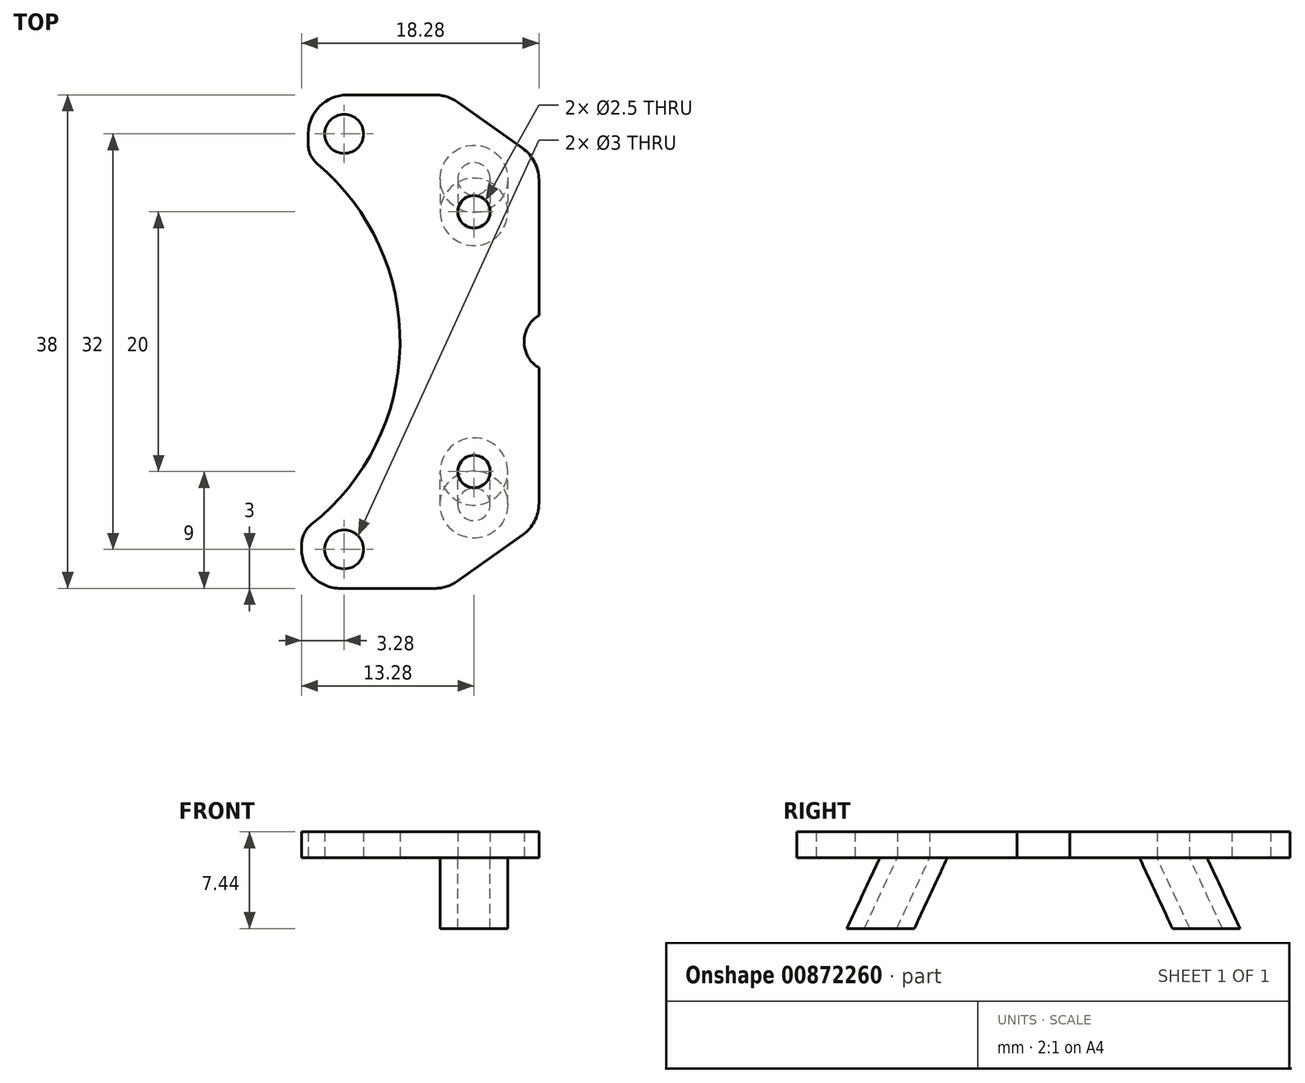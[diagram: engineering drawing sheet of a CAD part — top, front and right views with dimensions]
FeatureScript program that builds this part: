
annotation { "Feature Type Name" : "Feature", "Feature Type Description" : "" }
export const myFeature = defineFeature(function(context is Context, id is Id, definition is map)
    precondition{}
    {
        {
            var Q0;
            Q0=qCreatedBy(makeId("Top.planeOp"),FACE);
            var sketch = newSketch(context, id + "F0", { "sketchPlane" : qUnion([Q0])});
            skLineSegment(sketch, "E0.left", {"start": v(15, -12.45) * mm, "end": v(15, -2.03) * mm});
            skPoint(sketch, "E0.middle", {"position": v(0, 0) * mm});
            skPoint(sketch, "E1", {"position": v(0, 16) * mm});
            skPoint(sketch, "E2", {"position": v(0, -16) * mm});
            skCircle(sketch, "E3", {"center": v(0, 16) * mm, "radius": 1.5 * mm});
            skCircle(sketch, "E4", {"center": v(0, -16) * mm, "radius": 1.5 * mm});
            skPoint(sketch, "E5", {"position": v(10, 10) * mm});
            skPoint(sketch, "E6", {"position": v(10, -10) * mm});
            skCircle(sketch, "E7", {"center": v(10, 10) * mm, "radius": 2.6 * mm});
            skCircle(sketch, "E8", {"center": v(10, -10) * mm, "radius": 2.6 * mm});
            skPoint(sketch, "E0.right.end.orphan", {"position": v(-15, 22.5) * mm});
            skPoint(sketch, "E9.orphan", {"position": v(-15, -22.5) * mm});
            skPoint(sketch, "E10", {"position": v(4.82, 0) * mm});
            skPoint(sketch, "E10.positionSnap0", {"position": v(-5, 0) * mm});
            skPoint(sketch, "E11", {"position": v(-4.63, 15.5) * mm});
            skPoint(sketch, "E12", {"position": v(-4.63, -15.5) * mm});
            skArc(sketch, "E13", {"start": v(-2.5, -14.06) * mm, "mid": v(4.3, -0.29) * mm, "end": v(-2.06, 13.7) * mm});
            skLineSegment(sketch, "E14", {"start": v(8.72, 18.45) * mm, "end": v(13.73, 14.9) * mm});
            skLineSegment(sketch, "E15", {"start": v(8.72, -18.45) * mm, "end": v(13.73, -14.9) * mm});
            skPoint(sketch, "E16.orphan", {"position": v(15, 22.5) * mm});
            skPoint(sketch, "E17.orphan", {"position": v(15, -22.5) * mm});
            skLineSegment(sketch, "E18", {"start": v(-2.76, 16.05) * mm, "end": v(-2.77, 15.26) * mm});
            skLineSegment(sketch, "E19", {"start": v(0.24, 19) * mm, "end": v(6.98, 19) * mm});
            skLineSegment(sketch, "E20", {"start": v(-0.28, -19) * mm, "end": v(6.98, -19) * mm});
            skPoint(sketch, "E0.top.end.orphan", {"position": v(-5, 22.5) * mm});
            skPoint(sketch, "E21.orphan", {"position": v(3, 22.5) * mm});
            skPoint(sketch, "E22.start.orphan", {"position": v(-4.82, 19) * mm});
            skPoint(sketch, "E23.orphan", {"position": v(-4.82, -19) * mm});
            skPoint(sketch, "E24.orphan", {"position": v(-5, -22.5) * mm});
            skPoint(sketch, "E25.orphan", {"position": v(3, -22.5) * mm});
            skLineSegment(sketch, "E26.trimOffspring", {"start": v(-3.27, -15.6) * mm, "end": v(-3.27, -15.95) * mm});
            skPoint(sketch, "E27.visualSharp", {"position": v(-2.71, 19) * mm});
            skArc(sketch, "E27.filletArc", {"start": v(0.24, 19) * mm, "mid": v(-1.87, 18.14) * mm, "end": v(-2.76, 16.05) * mm});
            skPoint(sketch, "E28.visualSharp", {"position": v(-3.32, -19) * mm});
            skArc(sketch, "E28.filletArc", {"start": v(-3.27, -15.95) * mm, "mid": v(-2.41, -18.1) * mm, "end": v(-0.28, -19) * mm});
            skPoint(sketch, "E29.visualSharp", {"position": v(7.94, -19) * mm});
            skArc(sketch, "E29.filletArc", {"start": v(6.98, -19) * mm, "mid": v(7.9, -18.86) * mm, "end": v(8.72, -18.45) * mm});
            skPoint(sketch, "E30.visualSharp", {"position": v(15, -14) * mm});
            skArc(sketch, "E30.filletArc", {"start": v(13.73, -14.9) * mm, "mid": v(14.66, -13.83) * mm, "end": v(15, -12.45) * mm});
            skPoint(sketch, "E31.visualSharp", {"position": v(15, 14) * mm});
            skArc(sketch, "E31.filletArc", {"start": v(15, 12.45) * mm, "mid": v(14.66, 13.83) * mm, "end": v(13.73, 14.9) * mm});
            skPoint(sketch, "E32.visualSharp", {"position": v(7.94, 19) * mm});
            skArc(sketch, "E32.filletArc", {"start": v(8.72, 18.45) * mm, "mid": v(7.9, 18.86) * mm, "end": v(6.98, 19) * mm});
            skPoint(sketch, "E33.visualSharp", {"position": v(-2.79, 14.28) * mm});
            skArc(sketch, "E33.filletArc", {"start": v(-2.77, 15.26) * mm, "mid": v(-2.6, 14.4) * mm, "end": v(-2.06, 13.7) * mm});
            skPoint(sketch, "E34.visualSharp", {"position": v(-3.25, -14.61) * mm});
            skArc(sketch, "E34.filletArc", {"start": v(-2.5, -14.06) * mm, "mid": v(-3.06, -14.74) * mm, "end": v(-3.27, -15.6) * mm});
            skCircle(sketch, "E35", {"center": v(10, -10) * mm, "radius": 1.25 * mm});
            skCircle(sketch, "E36", {"center": v(10, 10) * mm, "radius": 1.25 * mm});
            skArc(sketch, "E37", {"start": v(15, 2.03) * mm, "mid": v(13.86, 0) * mm, "end": v(15, -2.03) * mm});
            skPoint(sketch, "E37.centerSnap0", {"position": v(15, 0) * mm});
            skLineSegment(sketch, "E38.trimOffspring", {"start": v(15, 2.03) * mm, "end": v(15, 12.45) * mm});
            skSolve(sketch);
        }
        {
            var Q0;
            Q0=makeQuery(id+"F0.imprint","IMPRINT",FACE,{"disambiguationData":[TD([[makeQuery(id+"F0.imprint","IMPRINT",EDGE,{"derivedFrom":sQuery(id+"F0.wireOp",EDGE,"E0.left")}),1.0]])]});
            var Q1;
            Q1=makeQuery(id+"F0.imprint","IMPRINT",FACE,{"disambiguationData":[TD([[makeQuery(id+"F0.imprint","IMPRINT",EDGE,{"derivedFrom":sQuery(id+"F0.wireOp",EDGE,"E8")}),1.0]])]});
            var Q2;
            Q2=makeQuery(id+"F0.imprint","IMPRINT",FACE,{"disambiguationData":[TD([[makeQuery(id+"F0.imprint","IMPRINT",EDGE,{"derivedFrom":sQuery(id+"F0.wireOp",EDGE,"E7")}),1.0]])]});
            extrude(context, id + "F1", {"entities" : qUnion([Q0, Q1, Q2]), "depth" : 2 * mm, "offsetDistance" : 25 * mm});
        }
        {
            var Q0;
            Q0=qCreatedBy(makeId("Right.planeOp"),FACE);
            cPlane(context, id + "F2", {"entities" : qUnion([Q0]), "cplaneType" : CPlaneType.OFFSET, "offset" : 10 * mm, "width" : 150 * mm, "height" : 150 * mm});
        }
        {
            var Q0;
            Q0=qCreatedBy(id+"F2.planeOp",FACE);
            var sketch = newSketch(context, id + "F3", { "sketchPlane" : qUnion([Q0])});
            skLineSegment(sketch, "E39", {"start": v(-12.55, 0) * mm, "end": v(-7.33, 0) * mm});
            skLineSegment(sketch, "E40", {"start": v(12.57, 0) * mm, "end": v(7.4, 0) * mm});
            skLineSegment(sketch, "E41", {"start": v(-7.33, 0) * mm, "end": v(-9.87, -5.44) * mm});
            skLineSegment(sketch, "E42", {"start": v(7.4, 0) * mm, "end": v(9.94, -5.44) * mm});
            skSolve(sketch);
        }
        {
            var Q0;
            Q0=makeQuery(id+"F0.imprint","IMPRINT",FACE,{"disambiguationData":[TD([[makeQuery(id+"F0.imprint","IMPRINT",EDGE,{"derivedFrom":sQuery(id+"F0.wireOp",EDGE,"E8")}),1.0]])]});
            var Q1;
            Q1=sQuery(id+"F3.wireOp",EDGE,"E41");
            sweep(context, id + "F4", {"operationType" : NewBodyOperationType.ADD, "profiles" : qUnion([Q0]), "path" : qUnion([Q1])});
        }
        {
            var Q0;
            Q0=makeQuery(id+"F0.imprint","IMPRINT",FACE,{"disambiguationData":[TD([[makeQuery(id+"F0.imprint","IMPRINT",EDGE,{"derivedFrom":sQuery(id+"F0.wireOp",EDGE,"E7")}),1.0]])]});
            var Q1;
            Q1=sQuery(id+"F3.wireOp",EDGE,"E42");
            sweep(context, id + "F5", {"operationType" : NewBodyOperationType.ADD, "profiles" : qUnion([Q0]), "path" : qUnion([Q1])});
        }
    });
